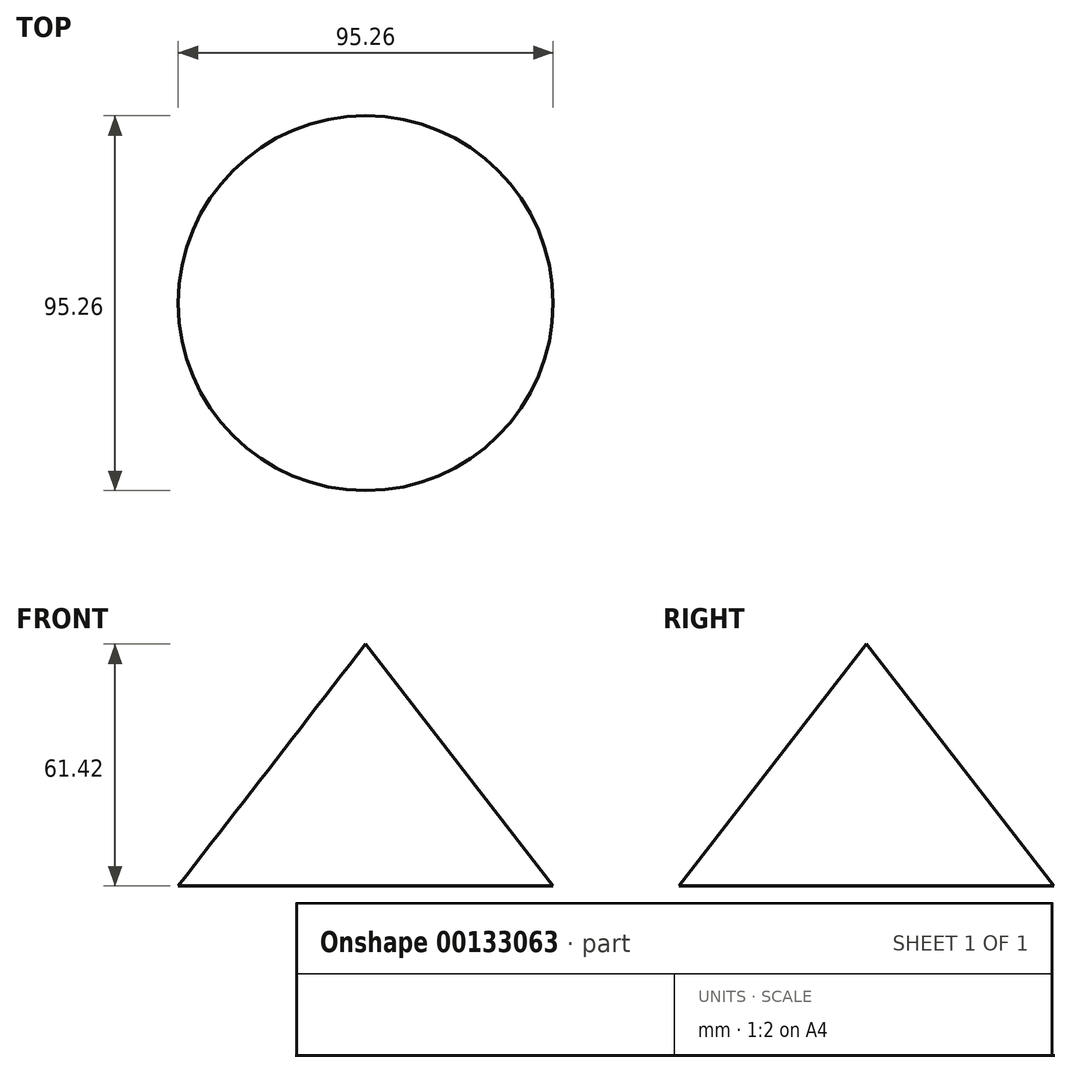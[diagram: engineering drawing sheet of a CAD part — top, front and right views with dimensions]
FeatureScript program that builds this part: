
annotation { "Feature Type Name" : "Feature", "Feature Type Description" : "" }
export const myFeature = defineFeature(function(context is Context, id is Id, definition is map)
    precondition{}
    {
        {
            var Q0;
            Q0=qCreatedBy(makeId("Front.planeOp"),FACE);
            var sketch = newSketch(context, id + "F0", { "sketchPlane" : qUnion([Q0])});
            skLineSegment(sketch, "E0", {"start": v(0, 0) * mm, "end": v(0, 61.42) * mm});
            skLineSegment(sketch, "E1", {"start": v(0, 61.42) * mm, "end": v(47.63, 0) * mm});
            skLineSegment(sketch, "E2", {"start": v(47.63, 0) * mm, "end": v(0, 0) * mm});
            skSolve(sketch);
        }
        {
            var Q0;
            Q0=makeQuery(id+"F0.imprint","IMPRINT",FACE,{"disambiguationData":[TD([[makeQuery(id+"F0.imprint","IMPRINT",EDGE,{"derivedFrom":sQuery(id+"F0.wireOp",EDGE,"E0")}),-1.0]])]});
            var Q1;
            Q1=sQuery(id+"F0.wireOp",EDGE,"E0");
            revolve(context, id + "F1", {"entities" : qUnion([Q0]), "axis" : qUnion([Q1]), "revolveType" : RevolveType.FULL});
        }
    });
